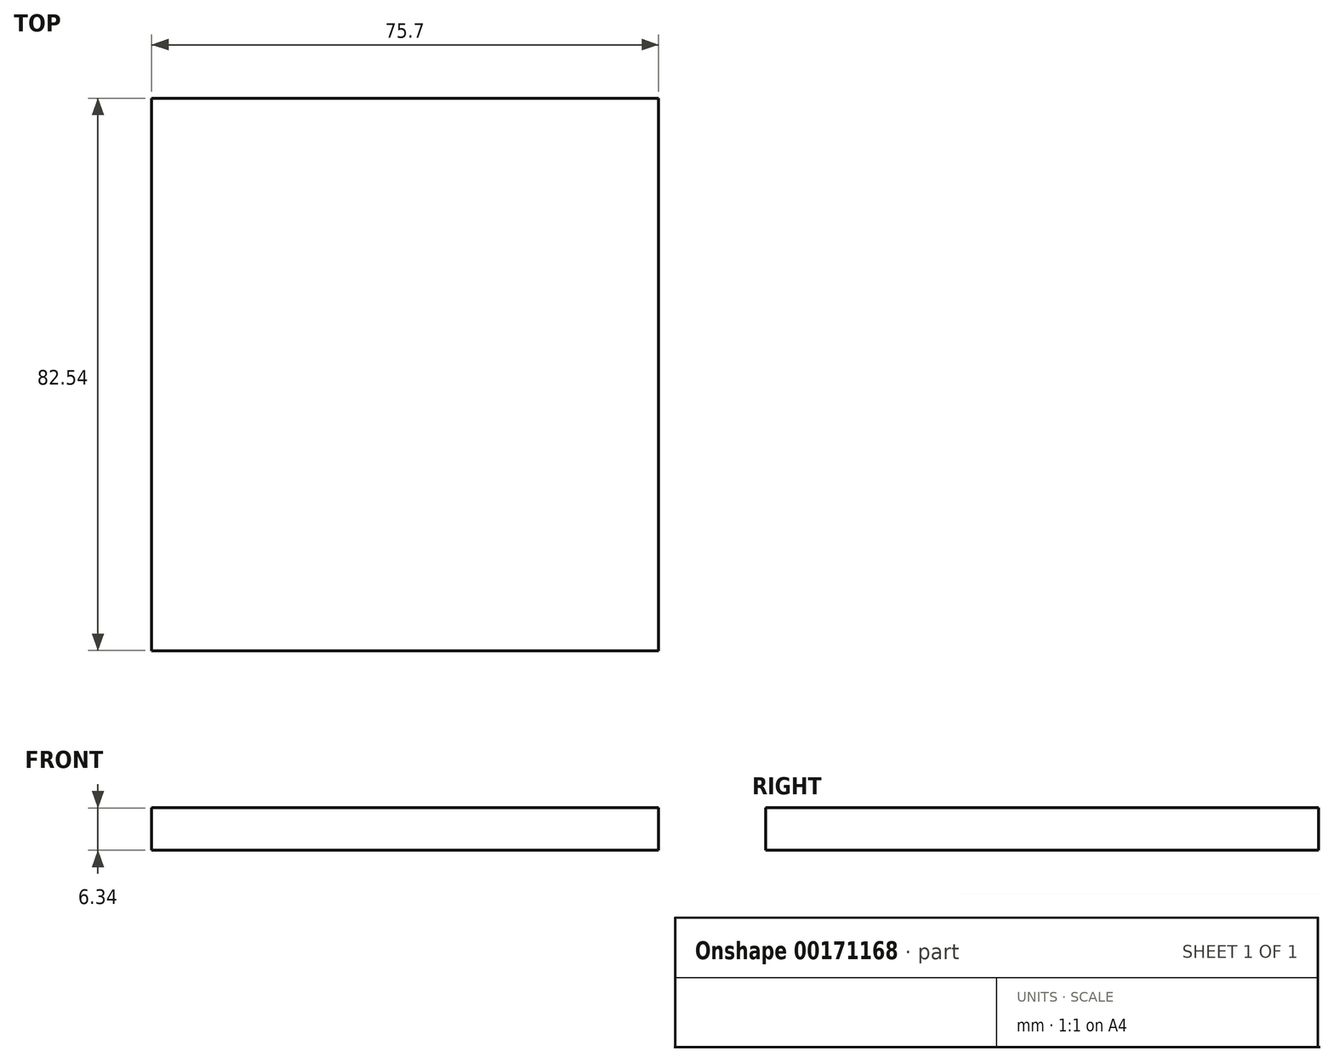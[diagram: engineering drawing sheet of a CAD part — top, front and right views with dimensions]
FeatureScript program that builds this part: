
annotation { "Feature Type Name" : "Feature", "Feature Type Description" : "" }
export const myFeature = defineFeature(function(context is Context, id is Id, definition is map)
    precondition{}
    {
        {
            var Q0;
            Q0=qCreatedBy(makeId("Top.planeOp"),FACE);
            var sketch = newSketch(context, id + "F0", { "sketchPlane" : qUnion([Q0])});
            skLineSegment(sketch, "E0.bottom", {"start": v(-37.85, 41.28) * mm, "end": v(37.85, 41.28) * mm});
            skLineSegment(sketch, "E0.top", {"start": v(-37.85, -41.28) * mm, "end": v(37.85, -41.28) * mm});
            skLineSegment(sketch, "E0.left", {"start": v(-37.85, 41.28) * mm, "end": v(-37.85, -41.28) * mm});
            skLineSegment(sketch, "E0.right", {"start": v(37.85, 41.28) * mm, "end": v(37.85, -41.28) * mm});
            skPoint(sketch, "E0.middle", {"position": v(0, 0) * mm});
            skSolve(sketch);
        }
        {
            var Q0;
            Q0=makeQuery(id+"F0.imprint","IMPRINT",FACE,{"disambiguationData":[TD([[makeQuery(id+"F0.imprint","IMPRINT",EDGE,{"derivedFrom":sQuery(id+"F0.wireOp",EDGE,"E0.bottom")}),-1.0]])]});
            extrude(context, id + "F1", {"entities" : qUnion([Q0]), "depth" : 6.35 * mm, "symmetric" : true});
        }
    });
